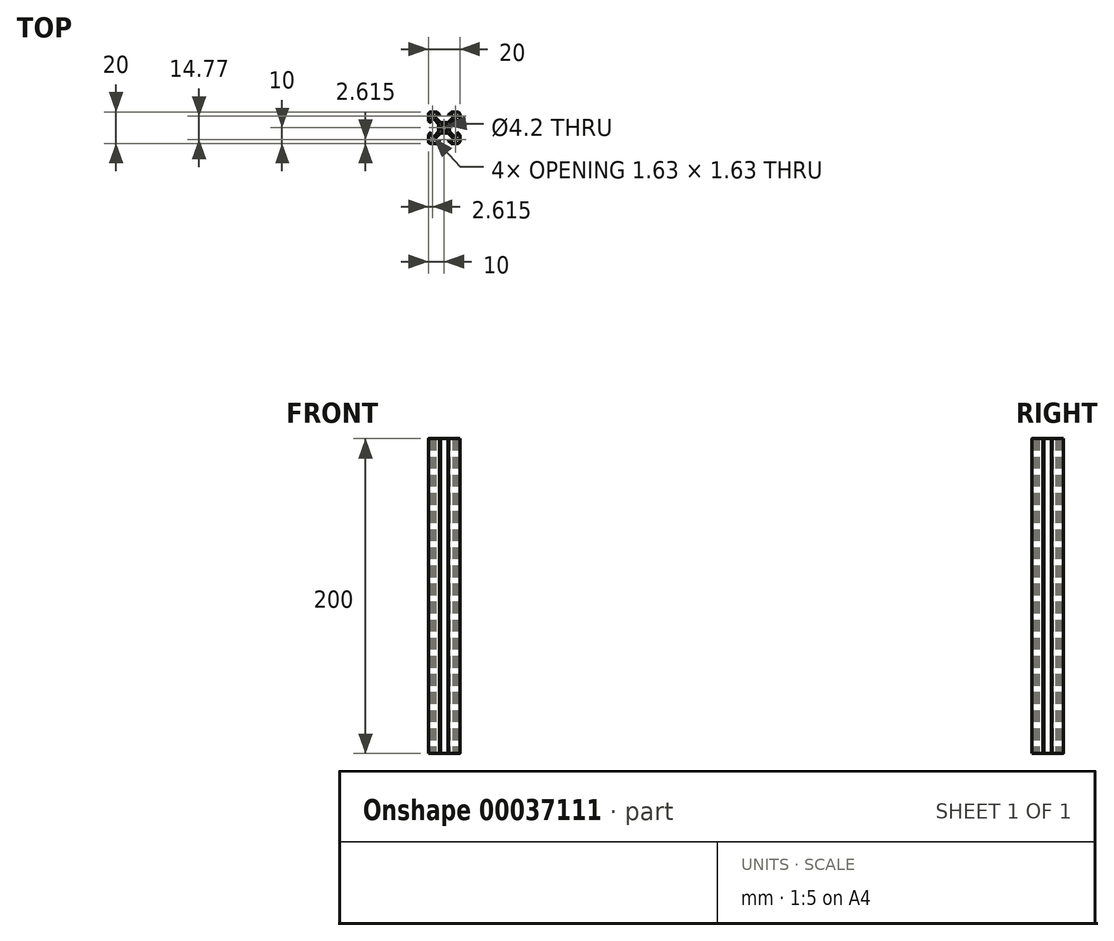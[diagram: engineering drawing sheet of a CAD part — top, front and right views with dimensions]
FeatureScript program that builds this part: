
annotation { "Feature Type Name" : "Feature", "Feature Type Description" : "" }
export const myFeature = defineFeature(function(context is Context, id is Id, definition is map)
    precondition{}
    {
        {
            var Q0;
            Q0=qCreatedBy(makeId("Top.planeOp"),FACE);
            var sketch = newSketch(context, id + "F0", { "sketchPlane" : qUnion([Q0])});
            skLineSegment(sketch, "E0", {"start": v(-8.2, -8.2) * mm, "end": v(-6.57, -8.2) * mm});
            skLineSegment(sketch, "E1", {"start": v(-8.2, -6.57) * mm, "end": v(-8.2, -8.2) * mm});
            skLineSegment(sketch, "E2", {"start": v(-7.66, -6.57) * mm, "end": v(-8.2, -6.57) * mm});
            skLineSegment(sketch, "E3", {"start": v(-6.57, -7.66) * mm, "end": v(-7.66, -6.57) * mm});
            skLineSegment(sketch, "E4", {"start": v(-6.57, -8.2) * mm, "end": v(-6.57, -7.66) * mm});
            skLineSegment(sketch, "E5", {"start": v(7.66, -6.57) * mm, "end": v(6.57, -7.66) * mm});
            skLineSegment(sketch, "E6", {"start": v(8.2, -6.57) * mm, "end": v(7.66, -6.57) * mm});
            skLineSegment(sketch, "E7", {"start": v(8.2, -8.2) * mm, "end": v(8.2, -6.57) * mm});
            skLineSegment(sketch, "E8", {"start": v(6.57, -8.2) * mm, "end": v(8.2, -8.2) * mm});
            skLineSegment(sketch, "E9", {"start": v(6.57, -7.66) * mm, "end": v(6.57, -8.2) * mm});
            skCircle(sketch, "E10", {"center": v(0, 0) * mm, "radius": 2.1 * mm});
            skLineSegment(sketch, "E11", {"start": v(8.2, 8.2) * mm, "end": v(6.57, 8.2) * mm});
            skLineSegment(sketch, "E12", {"start": v(8.2, 6.57) * mm, "end": v(8.2, 8.2) * mm});
            skLineSegment(sketch, "E13", {"start": v(7.66, 6.57) * mm, "end": v(8.2, 6.57) * mm});
            skLineSegment(sketch, "E14", {"start": v(6.57, 7.66) * mm, "end": v(7.66, 6.57) * mm});
            skLineSegment(sketch, "E15", {"start": v(6.57, 8.2) * mm, "end": v(6.57, 7.66) * mm});
            skLineSegment(sketch, "E16", {"start": v(-7.66, 6.57) * mm, "end": v(-6.57, 7.66) * mm});
            skLineSegment(sketch, "E17", {"start": v(-8.2, 6.57) * mm, "end": v(-7.66, 6.57) * mm});
            skLineSegment(sketch, "E18", {"start": v(-8.2, 8.2) * mm, "end": v(-8.2, 6.57) * mm});
            skLineSegment(sketch, "E19", {"start": v(-6.57, 8.2) * mm, "end": v(-8.2, 8.2) * mm});
            skLineSegment(sketch, "E20", {"start": v(-6.57, 7.66) * mm, "end": v(-6.57, 8.2) * mm});
            skLineSegment(sketch, "E21", {"start": v(-6.56, 5.5) * mm, "end": v(-3.4, 2.34) * mm});
            skLineSegment(sketch, "E22", {"start": v(-3.4, 2.34) * mm, "end": v(-3.4, -2.34) * mm});
            skLineSegment(sketch, "E23", {"start": v(-3.4, -2.34) * mm, "end": v(-6.56, -5.5) * mm});
            skLineSegment(sketch, "E24", {"start": v(-6.56, -5.5) * mm, "end": v(-8.2, -5.5) * mm});
            skLineSegment(sketch, "E25", {"start": v(-8.2, -5.5) * mm, "end": v(-8.2, -2.9) * mm});
            skLineSegment(sketch, "E26", {"start": v(-8.2, -2.9) * mm, "end": v(-8.31, -2.9) * mm});
            skLineSegment(sketch, "E27", {"start": v(-8.31, -2.9) * mm, "end": v(-9.77, -4.35) * mm});
            skArc(sketch, "E28", {"start": v(-9.77, -4.35) * mm, "mid": v(-9.94, -4.6) * mm, "end": v(-10, -4.9) * mm});
            skLineSegment(sketch, "E29", {"start": v(-10, -4.9) * mm, "end": v(-10, -8.5) * mm});
            skArc(sketch, "E30", {"start": v(-10, -8.5) * mm, "mid": v(-9.56, -9.56) * mm, "end": v(-8.5, -10) * mm});
            skLineSegment(sketch, "E31", {"start": v(-8.5, -10) * mm, "end": v(-4.9, -10) * mm});
            skArc(sketch, "E32", {"start": v(-4.9, -10) * mm, "mid": v(-4.6, -9.94) * mm, "end": v(-4.35, -9.77) * mm});
            skLineSegment(sketch, "E33", {"start": v(-4.35, -9.77) * mm, "end": v(-2.9, -8.31) * mm});
            skLineSegment(sketch, "E34", {"start": v(-2.9, -8.31) * mm, "end": v(-2.9, -8.2) * mm});
            skLineSegment(sketch, "E35", {"start": v(-2.9, -8.2) * mm, "end": v(-5.5, -8.2) * mm});
            skLineSegment(sketch, "E36", {"start": v(-5.5, -8.2) * mm, "end": v(-5.5, -6.56) * mm});
            skLineSegment(sketch, "E37", {"start": v(-5.5, -6.56) * mm, "end": v(-2.34, -3.4) * mm});
            skLineSegment(sketch, "E38", {"start": v(-2.34, -3.4) * mm, "end": v(2.34, -3.4) * mm});
            skLineSegment(sketch, "E39", {"start": v(2.34, -3.4) * mm, "end": v(5.5, -6.56) * mm});
            skLineSegment(sketch, "E40", {"start": v(5.5, -6.56) * mm, "end": v(5.5, -8.2) * mm});
            skLineSegment(sketch, "E41", {"start": v(5.5, -8.2) * mm, "end": v(2.9, -8.2) * mm});
            skLineSegment(sketch, "E42", {"start": v(2.9, -8.2) * mm, "end": v(2.9, -8.31) * mm});
            skLineSegment(sketch, "E43", {"start": v(2.9, -8.31) * mm, "end": v(4.35, -9.77) * mm});
            skArc(sketch, "E44", {"start": v(4.35, -9.77) * mm, "mid": v(4.6, -9.94) * mm, "end": v(4.9, -10) * mm});
            skLineSegment(sketch, "E45", {"start": v(4.9, -10) * mm, "end": v(8.5, -10) * mm});
            skArc(sketch, "E46", {"start": v(8.5, -10) * mm, "mid": v(9.56, -9.56) * mm, "end": v(10, -8.5) * mm});
            skLineSegment(sketch, "E47", {"start": v(10, -8.5) * mm, "end": v(10, -4.9) * mm});
            skArc(sketch, "E48", {"start": v(10, -4.9) * mm, "mid": v(9.94, -4.6) * mm, "end": v(9.77, -4.35) * mm});
            skLineSegment(sketch, "E49", {"start": v(9.77, -4.35) * mm, "end": v(8.31, -2.9) * mm});
            skLineSegment(sketch, "E50", {"start": v(8.31, -2.9) * mm, "end": v(8.2, -2.9) * mm});
            skLineSegment(sketch, "E51", {"start": v(8.2, -2.9) * mm, "end": v(8.2, -5.5) * mm});
            skLineSegment(sketch, "E52", {"start": v(8.2, -5.5) * mm, "end": v(6.56, -5.5) * mm});
            skLineSegment(sketch, "E53", {"start": v(6.56, -5.5) * mm, "end": v(3.4, -2.34) * mm});
            skLineSegment(sketch, "E54", {"start": v(3.4, -2.34) * mm, "end": v(3.4, 2.34) * mm});
            skLineSegment(sketch, "E55", {"start": v(3.4, 2.34) * mm, "end": v(6.56, 5.5) * mm});
            skLineSegment(sketch, "E56", {"start": v(6.56, 5.5) * mm, "end": v(8.2, 5.5) * mm});
            skLineSegment(sketch, "E57", {"start": v(8.2, 5.5) * mm, "end": v(8.2, 2.9) * mm});
            skLineSegment(sketch, "E58", {"start": v(8.2, 2.9) * mm, "end": v(8.31, 2.9) * mm});
            skLineSegment(sketch, "E59", {"start": v(8.31, 2.9) * mm, "end": v(9.77, 4.35) * mm});
            skArc(sketch, "E60", {"start": v(9.77, 4.35) * mm, "mid": v(9.94, 4.6) * mm, "end": v(10, 4.9) * mm});
            skLineSegment(sketch, "E61", {"start": v(10, 4.9) * mm, "end": v(10, 8.5) * mm});
            skArc(sketch, "E62", {"start": v(10, 8.5) * mm, "mid": v(9.56, 9.56) * mm, "end": v(8.5, 10) * mm});
            skLineSegment(sketch, "E63", {"start": v(8.5, 10) * mm, "end": v(4.9, 10) * mm});
            skArc(sketch, "E64", {"start": v(4.9, 10) * mm, "mid": v(4.6, 9.94) * mm, "end": v(4.35, 9.77) * mm});
            skLineSegment(sketch, "E65", {"start": v(4.35, 9.77) * mm, "end": v(2.9, 8.31) * mm});
            skLineSegment(sketch, "E66", {"start": v(2.9, 8.31) * mm, "end": v(2.9, 8.2) * mm});
            skLineSegment(sketch, "E67", {"start": v(2.9, 8.2) * mm, "end": v(5.5, 8.2) * mm});
            skLineSegment(sketch, "E68", {"start": v(5.5, 8.2) * mm, "end": v(5.5, 6.56) * mm});
            skLineSegment(sketch, "E69", {"start": v(5.5, 6.56) * mm, "end": v(2.34, 3.4) * mm});
            skLineSegment(sketch, "E70", {"start": v(2.34, 3.4) * mm, "end": v(-2.34, 3.4) * mm});
            skLineSegment(sketch, "E71", {"start": v(-2.34, 3.4) * mm, "end": v(-5.5, 6.56) * mm});
            skLineSegment(sketch, "E72", {"start": v(-5.5, 6.56) * mm, "end": v(-5.5, 8.2) * mm});
            skLineSegment(sketch, "E73", {"start": v(-5.5, 8.2) * mm, "end": v(-2.9, 8.2) * mm});
            skLineSegment(sketch, "E74", {"start": v(-2.9, 8.2) * mm, "end": v(-2.9, 8.31) * mm});
            skLineSegment(sketch, "E75", {"start": v(-2.9, 8.31) * mm, "end": v(-4.35, 9.77) * mm});
            skArc(sketch, "E76", {"start": v(-4.35, 9.77) * mm, "mid": v(-4.6, 9.94) * mm, "end": v(-4.9, 10) * mm});
            skLineSegment(sketch, "E77", {"start": v(-4.9, 10) * mm, "end": v(-8.5, 10) * mm});
            skArc(sketch, "E78", {"start": v(-8.5, 10) * mm, "mid": v(-9.56, 9.56) * mm, "end": v(-10, 8.5) * mm});
            skLineSegment(sketch, "E79", {"start": v(-10, 8.5) * mm, "end": v(-10, 4.9) * mm});
            skArc(sketch, "E80", {"start": v(-10, 4.9) * mm, "mid": v(-9.94, 4.6) * mm, "end": v(-9.77, 4.35) * mm});
            skLineSegment(sketch, "E81", {"start": v(-9.77, 4.35) * mm, "end": v(-8.31, 2.9) * mm});
            skLineSegment(sketch, "E82", {"start": v(-8.31, 2.9) * mm, "end": v(-8.2, 2.9) * mm});
            skLineSegment(sketch, "E83", {"start": v(-8.2, 2.9) * mm, "end": v(-8.2, 5.5) * mm});
            skLineSegment(sketch, "E84", {"start": v(-8.2, 5.5) * mm, "end": v(-6.56, 5.5) * mm});
            skSolve(sketch);
        }
        {
            var Q0;
            Q0=qSketchRegion(id+"F0",true);
            extrude(context, id + "F1", {"entities" : qUnion([Q0]), "depth" : 200 * mm});
        }
    });
